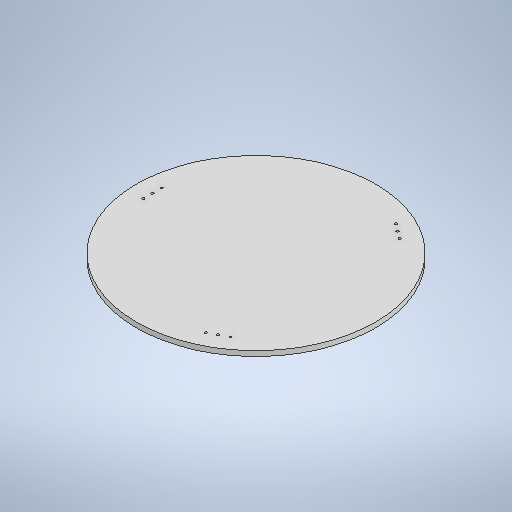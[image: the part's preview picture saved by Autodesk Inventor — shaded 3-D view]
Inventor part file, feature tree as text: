
AUTODESK INVENTOR PART (.ipt)
format: ipt  version: 2025.1 (Build 291241000, 241)  size: 274,432 bytes
history: native  units: mm
features: sketch x3, extrude x2
ambient origin geometry x8: Origin, YZ Plane, XZ Plane, XY Plane, X Axis, Y Axis, Z Axis, Center Point
bodies: Solid1 (feature_tree)
feature tree (5):
  sketch  "Sketch1"  dims[d20=300.0mm d22=120.0deg]
  extrude  "Extrusion1"  TaperAngle=120.0deg  [1 undecoded]
  extrude  "Extrusion3"  Depth=1.0mm
  sketch  "Sketch7"  dims[d25=10.33mm d26=20.066mm d27=3.0mm d28=20.066mm d29=3.0mm d30=20.066mm d31=3.0mm d32=6.35mm d33=0.0mm d36=10.0mm d37=10.0mm d38=3.0mm d39=3.0mm d40=10.0mm d41=10.0mm d42=3.0mm d43=3.0mm d44=10.0mm d45=10.0mm d46=3.0mm d47=3.0mm d48=0.0mm d49=0.0mm d34=0.5mm d35=0.872665mm d50=0.5mm d51=0.872665mm d52=0.5mm d53=0.872665mm]
  sketch  "Sketch2"  dims[d23=120.0deg d24=1.0mm]
note: 1 required parameter value undecoded (feature->parameter linkage not recoverable at this tier; creation-order binding heuristic only, values carry confidence <= 0.55)
